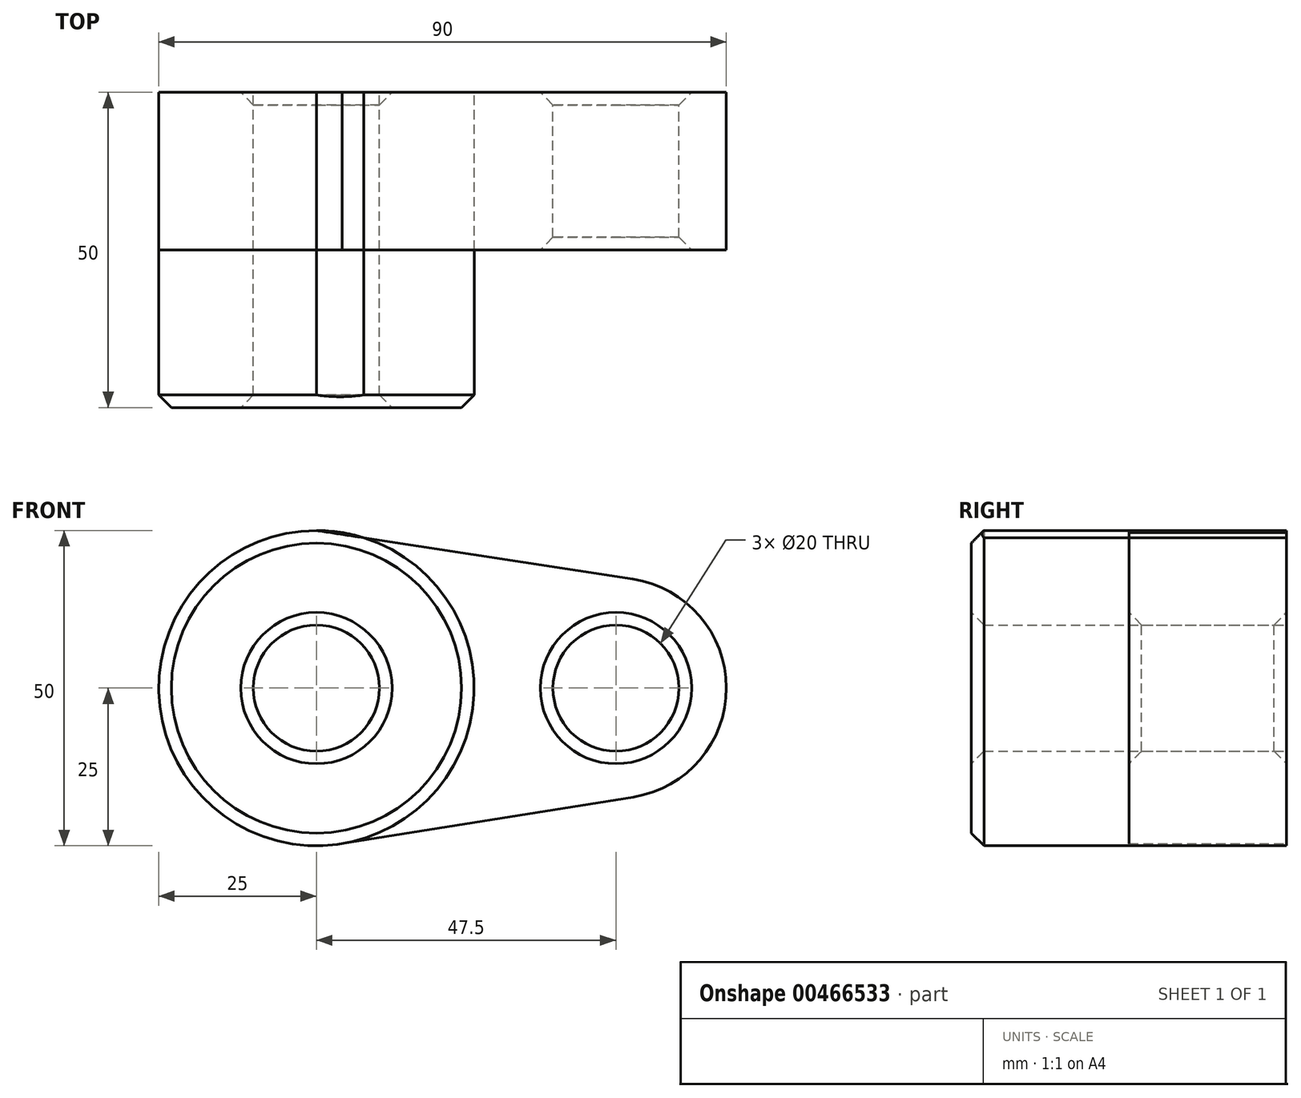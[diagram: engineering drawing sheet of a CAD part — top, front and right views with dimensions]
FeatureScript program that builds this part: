
annotation { "Feature Type Name" : "Feature", "Feature Type Description" : "" }
export const myFeature = defineFeature(function(context is Context, id is Id, definition is map)
    precondition{}
    {
        {
            var Q0;
            Q0=qCreatedBy(makeId("Front.planeOp"),FACE);
            var sketch = newSketch(context, id + "F0", { "sketchPlane" : qUnion([Q0])});
            skCircle(sketch, "E0", {"center": v(0, 0) * mm, "radius": 25 * mm});
            skCircle(sketch, "E1", {"center": v(47.5, 0) * mm, "radius": 17.5 * mm});
            skLineSegment(sketch, "E2", {"start": v(0, 25) * mm, "end": v(50.16, 17.3) * mm});
            skLineSegment(sketch, "E3", {"start": v(3.95, -24.69) * mm, "end": v(50.26, -17.28) * mm});
            skCircle(sketch, "E4", {"center": v(0, 0) * mm, "radius": 10 * mm});
            skCircle(sketch, "E5", {"center": v(47.5, 0) * mm, "radius": 10 * mm});
            skSolve(sketch);
        }
        {
            var Q0;
            Q0 = qSketchRegion(id + "F0", true);
            extrude(context, id + "F1", {"entities" : qUnion([Q0]), "depth" : 25 * mm});
        }
        {
            var Q0;
            Q0=makeQuery(id+"F0.imprint","IMPRINT",FACE,{"disambiguationData":[TD([[makeQuery(id+"F0.imprint","IMPRINT",EDGE,{"derivedFrom":sQuery(id+"F0.wireOp",EDGE,"E4")}),-1.0]])]});
            extrude(context, id + "F2", {"entities" : qUnion([Q0]), "operationType" : NewBodyOperationType.ADD, "depth" : 50 * mm});
        }
        {
            var Q0;
            Q0=makeQuery(id+"F2.opExtrude","CAP_EDGE",EDGE,{"disambiguationData":[OSD([sQuery(id+"F0.wireOp",EDGE,"E0")])],"isStart":false});
            var Q1;
            Q1=makeQuery(id+"F2.opExtrude","CAP_EDGE",EDGE,{"disambiguationData":[OSD([sQuery(id+"F0.wireOp",EDGE,"E4")])],"isStart":false});
            var Q2;
            Q2=makeQuery(id+"F1.opExtrude","CAP_EDGE",EDGE,{"disambiguationData":[OSD([sQuery(id+"F0.wireOp",EDGE,"E5")])],"isStart":false});
            chamfer(context, id + "F3", {"entities" : qUnion([Q0, Q1, Q2]), "width" : 2 * mm, "tangentPropagation" : true});
        }
        {
            var Q0;
            Q0=makeQuery(id+"F1.opExtrude","CAP_EDGE",EDGE,{"disambiguationData":[OSD([sQuery(id+"F0.wireOp",EDGE,"E4")])],"isStart":true});
            var Q1;
            Q1=makeQuery(id+"F1.opExtrude","CAP_EDGE",EDGE,{"disambiguationData":[OSD([sQuery(id+"F0.wireOp",EDGE,"E5")])],"isStart":true});
            chamfer(context, id + "F4", {"entities" : qUnion([Q0, Q1]), "width" : 2 * mm, "tangentPropagation" : true});
        }
        {
            var Q0;
            Q0=qCreatedBy(makeId("Front.planeOp"),FACE);
            var sketch = newSketch(context, id + "F5", { "sketchPlane" : qUnion([Q0])});
            skCircle(sketch, "E6", {"center": v(0, 0) * mm, "radius": 25 * mm});
            skCircle(sketch, "E7", {"center": v(90, 0) * mm, "radius": 17.5 * mm});
            skLineSegment(sketch, "E8", {"start": v(0, 25) * mm, "end": v(90, 17.56) * mm});
            skLineSegment(sketch, "E9", {"start": v(0, -25) * mm, "end": v(91.44, -17.44) * mm});
            skCircle(sketch, "E10", {"center": v(0, 0) * mm, "radius": 10 * mm});
            skCircle(sketch, "E11", {"center": v(90, 0) * mm, "radius": 10 * mm});
            skSolve(sketch);
        }
        {
            var Q0;
            Q0=makeQuery(id+"F5.imprint","IMPRINT",FACE,{"disambiguationData":[TD([[makeQuery(id+"F5.imprint","IMPRINT",EDGE,{"derivedFrom":sQuery(id+"F5.wireOp",EDGE,"E10")}),-1.0]])]});
            extrude(context, id + "F6", {"entities" : qUnion([Q0]), "depth" : 25 * mm});
        }
    });
